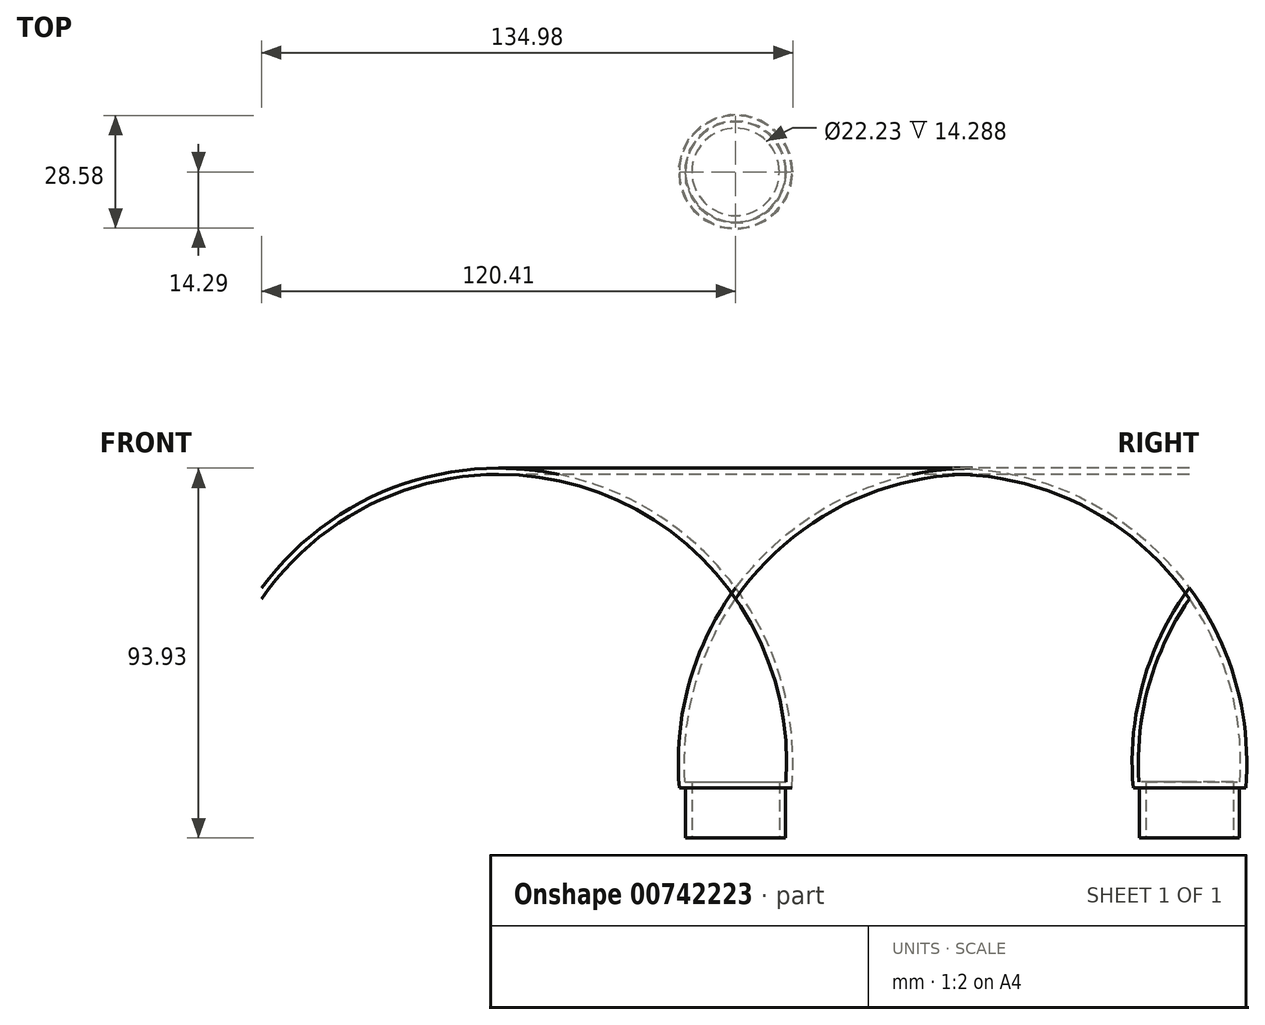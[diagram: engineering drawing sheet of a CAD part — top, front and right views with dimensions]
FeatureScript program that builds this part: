
annotation { "Feature Type Name" : "Feature", "Feature Type Description" : "" }
export const myFeature = defineFeature(function(context is Context, id is Id, definition is map)
    precondition{}
    {
        {
            var Q0;
            Q0=qCreatedBy(makeId("Front.planeOp"),FACE);
            var sketch = newSketch(context, id + "F0", { "sketchPlane" : qUnion([Q0])});
            skLineSegment(sketch, "E0", {"start": v(0, 0) * mm, "end": v(0, 63.5) * mm});
            skLineSegment(sketch, "E1", {"start": v(0, 0) * mm, "end": v(12.7, 0) * mm});
            skLineSegment(sketch, "E2", {"start": v(12.7, 0) * mm, "end": v(12.7, 12.7) * mm});
            skLineSegment(sketch, "E3", {"start": v(12.7, 12.7) * mm, "end": v(14.29, 12.7) * mm});
            skArc(sketch, "E4", {"start": v(14.29, 12.7) * mm, "mid": v(11.77, 39.4) * mm, "end": v(0, 63.5) * mm});
            skArc(sketch, "E5.0", {"start": v(12.82, 14.29) * mm, "mid": v(10.35, 38.61) * mm, "end": v(0, 60.77) * mm});
            skLineSegment(sketch, "E5.1", {"start": v(11.11, 14.29) * mm, "end": v(12.82, 14.29) * mm});
            skLineSegment(sketch, "E5.2", {"start": v(11.11, 0) * mm, "end": v(11.11, 14.29) * mm});
            skSolve(sketch);
        }
        {
            var Q0;
            {var subQ0=sQuery(id+"F0.wireOp",EDGE,"E2");Q0=makeQuery(id+"F0.imprint","IMPRINT",FACE,{"disambiguationData":[TD([[makeQuery(id+"F0.imprint","IMPRINT",EDGE,{"derivedFrom":subQ0}),1.0]])]});}
            var Q1;
            Q1=sQuery(id+"F0.wireOp",EDGE,"E0");
            revolve(context, id + "F1", {"surfaceOperationType" : NewSurfaceOperationType.NEW, "entities" : qUnion([Q0]), "axis" : qUnion([Q1]), "revolveType" : RevolveType.FULL});
        }
    });
